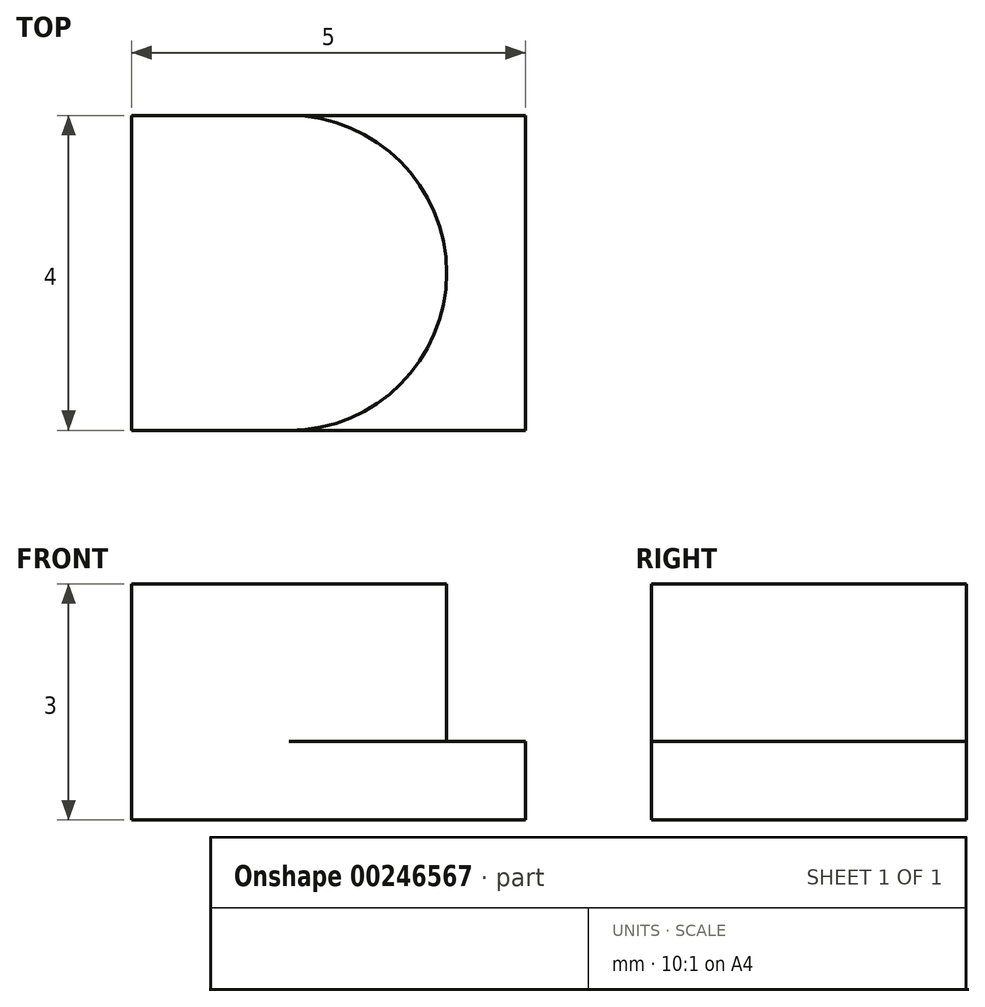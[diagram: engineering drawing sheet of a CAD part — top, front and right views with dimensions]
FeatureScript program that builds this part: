
annotation { "Feature Type Name" : "Feature", "Feature Type Description" : "" }
export const myFeature = defineFeature(function(context is Context, id is Id, definition is map)
    precondition{}
    {
        {
            var Q0;
            Q0=qCreatedBy(makeId("Top.planeOp"),FACE);
            var sketch = newSketch(context, id + "F0", { "sketchPlane" : qUnion([Q0])});
            skLineSegment(sketch, "E0.bottom", {"start": v(0, 0) * mm, "end": v(5, 0) * mm});
            skLineSegment(sketch, "E0.top", {"start": v(0, 4) * mm, "end": v(5, 4) * mm});
            skLineSegment(sketch, "E0.left", {"start": v(0, 0) * mm, "end": v(0, 4) * mm});
            skLineSegment(sketch, "E0.right", {"start": v(5, 0) * mm, "end": v(5, 4) * mm});
            skSolve(sketch);
        }
        {
            var Q0;
            Q0=makeQuery(id+"F0.imprint","IMPRINT",FACE,{"disambiguationData":[TD([[makeQuery(id+"F0.imprint","IMPRINT",EDGE,{"derivedFrom":sQuery(id+"F0.wireOp",EDGE,"E0.bottom")}),1.0]])]});
            extrude(context, id + "F1", {"entities" : qUnion([Q0]), "depth" : 1 * mm});
        }
        {
            var Q0;
            Q0=makeQuery(id+"F1.opExtrude","CAP_FACE",FACE,{"disambiguationData":[OSD([sQuery(id+"F0.wireOp",EDGE,"E0.bottom"),sQuery(id+"F0.wireOp",EDGE,"E0.top"),sQuery(id+"F0.wireOp",EDGE,"E0.left"),sQuery(id+"F0.wireOp",EDGE,"E0.right")])],"isStart":false});
            var sketch = newSketch(context, id + "F2", { "sketchPlane" : qUnion([Q0])});
            skArc(sketch, "E1", {"start": v(2, 0) * mm, "mid": v(4, 2) * mm, "end": v(2, 4) * mm});
            skLineSegment(sketch, "E2", {"start": v(0, 4) * mm, "end": v(2, 4) * mm});
            skLineSegment(sketch, "E3", {"start": v(0, 0) * mm, "end": v(2, 0) * mm});
            skLineSegment(sketch, "E4", {"start": v(0, 4) * mm, "end": v(0, 0) * mm});
            skSolve(sketch);
        }
        {
            var Q0;
            Q0=makeQuery(id+"F2.imprint","IMPRINT",FACE,{"disambiguationData":[TD([[makeQuery(id+"F2.imprint","IMPRINT",EDGE,{"derivedFrom":sQuery(id+"F2.wireOp",EDGE,"E1")}),1.0]])]});
            extrude(context, id + "F3", {"entities" : qUnion([Q0]), "operationType" : NewBodyOperationType.ADD, "depth" : 2 * mm});
        }
    });
